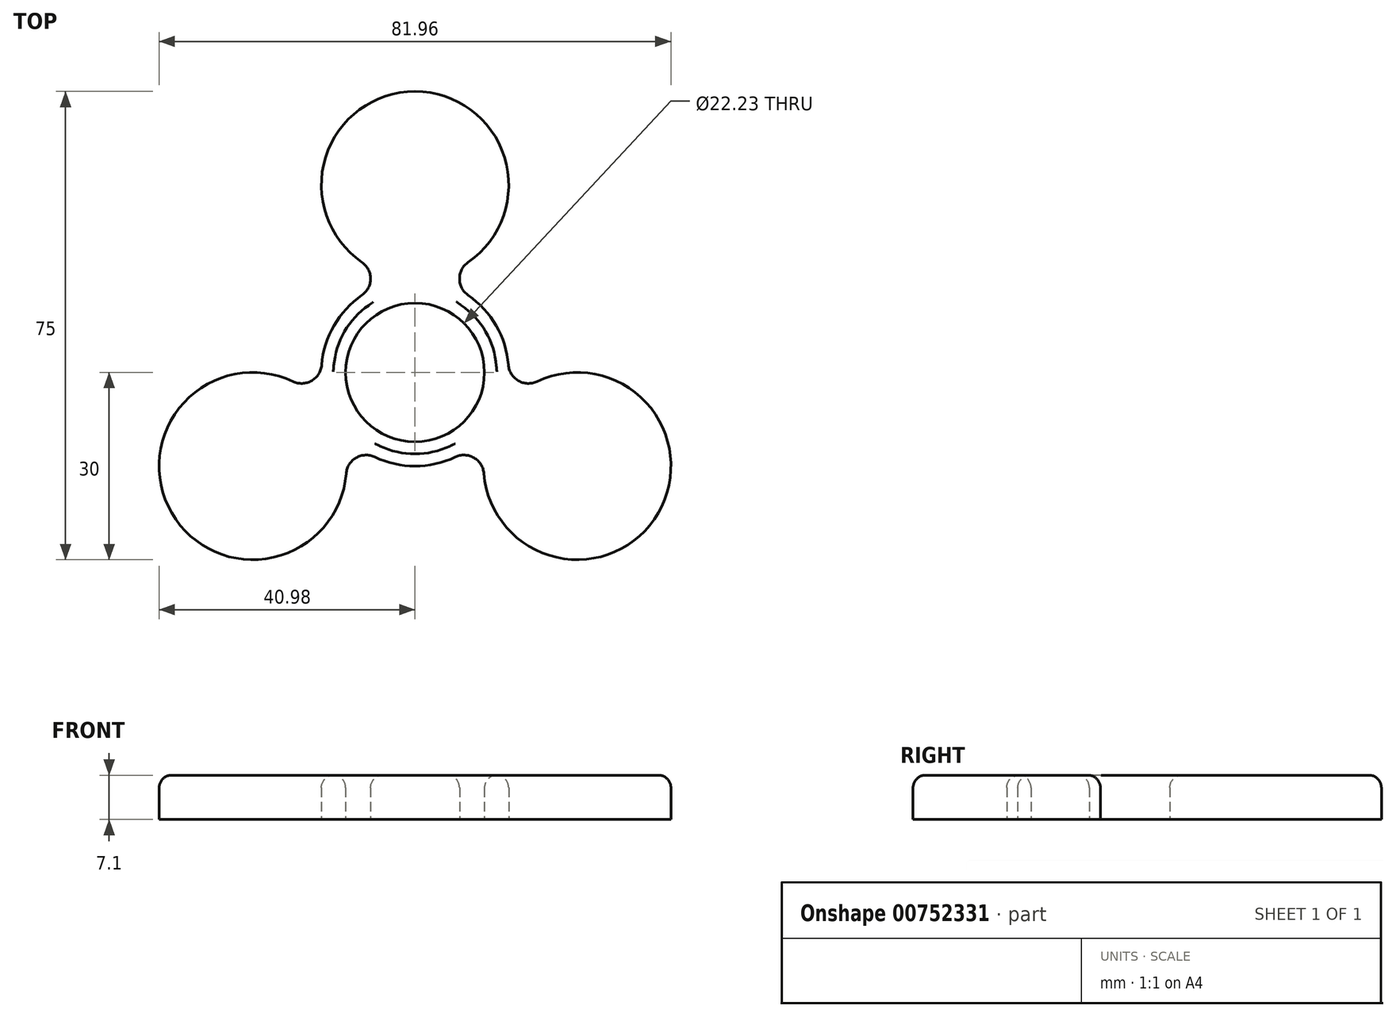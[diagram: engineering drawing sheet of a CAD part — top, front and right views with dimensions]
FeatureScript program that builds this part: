
annotation { "Feature Type Name" : "Feature", "Feature Type Description" : "" }
export const myFeature = defineFeature(function(context is Context, id is Id, definition is map)
    precondition{}
    {
        {
            var Q0;
            Q0=qCreatedBy(makeId("Top.planeOp"),FACE);
            var sketch = newSketch(context, id + "F0", { "sketchPlane" : qUnion([Q0])});
            skCircle(sketch, "E0", {"center": v(0, 0) * mm, "radius": 11.11 * mm});
            skCircle(sketch, "E1", {"center": v(0, 0) * mm, "radius": 15 * mm});
            skSolve(sketch);
        }
        {
            var Q0;
            Q0 = qSketchRegion(id + "F0", true);
            extrude(context, id + "F1", {"entities" : qUnion([Q0]), "depth" : 7.1 * mm, "offsetDistance" : 25 * mm});
        }
        {
            var Q0;
            Q0=qCreatedBy(makeId("Top.planeOp"),FACE);
            var sketch = newSketch(context, id + "F2", { "sketchPlane" : qUnion([Q0])});
            skCircle(sketch, "E2", {"center": v(0, 30) * mm, "radius": 15 * mm});
            skCircle(sketch, "E3.1.0", {"center": v(-25.98, -15) * mm, "radius": 15 * mm});
            skCircle(sketch, "E3.2.0", {"center": v(25.98, -15) * mm, "radius": 15 * mm});
            skPoint(sketch, "E3.center", {"position": v(0, 0) * mm});
            skSolve(sketch);
        }
        {
            var Q0;
            Q0 = qSketchRegion(id + "F2", true);
            extrude(context, id + "F3", {"entities" : qUnion([Q0]), "operationType" : NewBodyOperationType.ADD, "depth" : 7.1 * mm, "offsetDistance" : 25 * mm});
        }
        {
            var Q0;
            Q0=qCreatedBy(makeId("Top.planeOp"),FACE);
            var sketch = newSketch(context, id + "F4", { "sketchPlane" : qUnion([Q0])});
            skArc(sketch, "E4", {"start": v(-8.52, 12.35) * mm, "mid": v(-7.12, 15) * mm, "end": v(-8.52, 17.65) * mm});
            skArc(sketch, "E5.MirrorCS", {"start": v(8.52, 12.35) * mm, "mid": v(7.12, 15) * mm, "end": v(8.52, 17.65) * mm});
            skArc(sketch, "E6", {"start": v(8.52, 12.35) * mm, "mid": v(0, 15) * mm, "end": v(-8.52, 12.35) * mm});
            skArc(sketch, "E7", {"start": v(-8.52, 17.65) * mm, "mid": v(0, 15) * mm, "end": v(8.52, 17.65) * mm});
            skArc(sketch, "E8.1.0", {"start": v(-14.95, 1.2) * mm, "mid": v(-16.55, -1.33) * mm, "end": v(-19.54, -1.45) * mm});
            skArc(sketch, "E8.1.1", {"start": v(-14.95, 1.2) * mm, "mid": v(-13, -7.5) * mm, "end": v(-6.44, -13.55) * mm});
            skArc(sketch, "E8.1.2", {"start": v(-6.44, -13.55) * mm, "mid": v(-9.43, -13.67) * mm, "end": v(-11.03, -16.2) * mm});
            skArc(sketch, "E8.1.3", {"start": v(-11.03, -16.2) * mm, "mid": v(-13, -7.5) * mm, "end": v(-19.54, -1.45) * mm});
            skArc(sketch, "E8.2.0", {"start": v(6.44, -13.55) * mm, "mid": v(9.43, -13.67) * mm, "end": v(11.03, -16.2) * mm});
            skArc(sketch, "E8.2.1", {"start": v(6.44, -13.55) * mm, "mid": v(13, -7.5) * mm, "end": v(14.95, 1.2) * mm});
            skArc(sketch, "E8.2.2", {"start": v(14.95, 1.2) * mm, "mid": v(16.55, -1.33) * mm, "end": v(19.54, -1.45) * mm});
            skArc(sketch, "E8.2.3", {"start": v(19.54, -1.45) * mm, "mid": v(13, -7.5) * mm, "end": v(11.03, -16.2) * mm});
            skSolve(sketch);
        }
        {
            var Q0;
            Q0 = qSketchRegion(id + "F4", true);
            extrude(context, id + "F5", {"entities" : qUnion([Q0]), "operationType" : NewBodyOperationType.ADD, "depth" : 7.1 * mm, "offsetDistance" : 25 * mm});
        }
        {
            var Q0;
            {var subQ0=sQuery(id+"F4.wireOp",EDGE,"E8.2.3");var subQ1=sQuery(id+"F4.wireOp",EDGE,"E8.2.1");var subQ2=sQuery(id+"F4.wireOp",EDGE,"E8.1.3");var subQ3=sQuery(id+"F4.wireOp",EDGE,"E8.1.1");var subQ4=sQuery(id+"F4.wireOp",EDGE,"E7");var subQ5=sQuery(id+"F4.wireOp",EDGE,"E6");Q0=makeQuery(id+"F5.boolean.opBoolean","MERGE",FACE,{"derivedFrom":[makeQuery(id+"F1.opExtrude","CAP_FACE",FACE,{"disambiguationData":[OSD([sQuery(id+"F0.wireOp",EDGE,"E0"),sQuery(id+"F0.wireOp",EDGE,"E1")])],"isStart":false}),makeQuery(id+"F3.opExtrude","CAP_FACE",FACE,{"disambiguationData":[OSD([sQuery(id+"F2.wireOp",EDGE,"E2")])],"isStart":false}),makeQuery(id+"F3.opExtrude","CAP_FACE",FACE,{"disambiguationData":[OSD([sQuery(id+"F2.wireOp",EDGE,"E3.1.0")])],"isStart":false}),makeQuery(id+"F3.opExtrude","CAP_FACE",FACE,{"disambiguationData":[OSD([sQuery(id+"F2.wireOp",EDGE,"E3.2.0")])],"isStart":false}),makeQuery(id+"F5.opExtrude","CAP_FACE",FACE,{"disambiguationData":[OSD([sQuery(id+"F4.wireOp",EDGE,"E4"),subQ5,subQ4])],"isStart":false}),makeQuery(id+"F5.opExtrude","CAP_FACE",FACE,{"disambiguationData":[OSD([sQuery(id+"F4.wireOp",EDGE,"E5.MirrorCS"),subQ5,subQ4])],"isStart":false}),makeQuery(id+"F5.opExtrude","CAP_FACE",FACE,{"disambiguationData":[OSD([sQuery(id+"F4.wireOp",EDGE,"E8.1.0"),subQ3,subQ2])],"isStart":false}),makeQuery(id+"F5.opExtrude","CAP_FACE",FACE,{"disambiguationData":[OSD([subQ3,sQuery(id+"F4.wireOp",EDGE,"E8.1.2"),subQ2])],"isStart":false}),makeQuery(id+"F5.opExtrude","CAP_FACE",FACE,{"disambiguationData":[OSD([sQuery(id+"F4.wireOp",EDGE,"E8.2.0"),subQ1,subQ0])],"isStart":false}),makeQuery(id+"F5.opExtrude","CAP_FACE",FACE,{"disambiguationData":[OSD([subQ1,sQuery(id+"F4.wireOp",EDGE,"E8.2.2"),subQ0])],"isStart":false})]});}
            fillet(context, id + "F6", {"entities" : qUnion([Q0]), "radius" : 2 * mm, "tangentPropagation" : true, "allowEdgeOverflow" : false});
        }
    });
